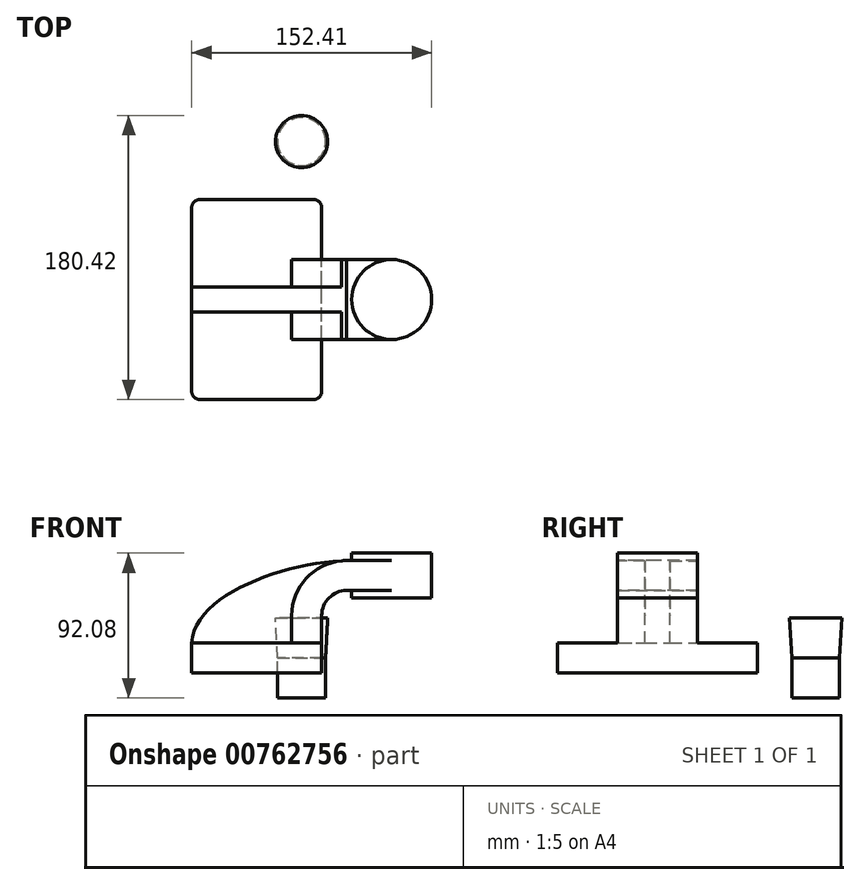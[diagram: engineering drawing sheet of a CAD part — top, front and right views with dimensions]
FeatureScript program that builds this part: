
annotation { "Feature Type Name" : "Feature", "Feature Type Description" : "" }
export const myFeature = defineFeature(function(context is Context, id is Id, definition is map)
    precondition{}
    {
        {
            var Q0;
            Q0=qCreatedBy(makeId("Front.planeOp"),FACE);
            var sketch = newSketch(context, id + "F0", { "sketchPlane" : qUnion([Q0])});
            skLineSegment(sketch, "E0.rect.bottom", {"start": v(-41.28, 9.52) * mm, "end": v(41.28, 9.52) * mm});
            skLineSegment(sketch, "E0.rect.top", {"start": v(-41.28, -9.52) * mm, "end": v(41.28, -9.52) * mm});
            skLineSegment(sketch, "E0.rect.left", {"start": v(-41.28, 9.52) * mm, "end": v(-41.28, -9.52) * mm});
            skLineSegment(sketch, "E0.rect.right", {"start": v(41.28, 9.52) * mm, "end": v(41.28, -9.52) * mm});
            skPoint(sketch, "E0.rect.middle", {"position": v(0, 0) * mm});
            skLineSegment(sketch, "E1", {"start": v(41.28, 9.52) * mm, "end": v(41.28, 27) * mm});
            skArc(sketch, "E2", {"start": v(41.28, 27) * mm, "mid": v(45.92, 38.23) * mm, "end": v(57.15, 42.88) * mm});
            skLineSegment(sketch, "E3", {"start": v(57.15, 42.88) * mm, "end": v(85.72, 42.88) * mm});
            skLineSegment(sketch, "E4.rect.bottom", {"start": v(60.32, 38.1) * mm, "end": v(111.12, 38.1) * mm});
            skLineSegment(sketch, "E4.rect.top", {"start": v(60.32, 66.68) * mm, "end": v(111.12, 66.68) * mm});
            skLineSegment(sketch, "E4.rect.left", {"start": v(60.32, 38.1) * mm, "end": v(60.32, 66.68) * mm});
            skLineSegment(sketch, "E4.rect.right", {"start": v(111.13, 38.1) * mm, "end": v(111.12, 66.68) * mm});
            skPoint(sketch, "E4.rect.middle", {"position": v(85.72, 52.39) * mm});
            skLineSegment(sketch, "E5.0", {"start": v(57.15, 61.93) * mm, "end": v(85.72, 61.93) * mm});
            skArc(sketch, "E5.1", {"start": v(22.23, 27) * mm, "mid": v(32.45, 51.7) * mm, "end": v(57.15, 61.93) * mm});
            skLineSegment(sketch, "E5.2", {"start": v(22.23, 9.52) * mm, "end": v(22.23, 27) * mm});
            skLineSegment(sketch, "E6", {"start": v(85.72, 38.1) * mm, "end": v(85.72, 66.68) * mm});
            skFitSpline(sketch, "E7", {"points": [v(-41.28, 9.53) * mm, v(57.15, 61.93) * mm], "startDerivative": vector(5.2, 92.34) * mm, "endDerivative": vector(120.92, 4.22) * mm});
            skSolve(sketch);
        }
        {
            var Q0;
            Q0=makeQuery(id+"F0.imprint","IMPRINT",FACE,{"disambiguationData":[TD([[makeQuery(id+"F0.imprint","IMPRINT",EDGE,{"derivedFrom":sQuery(id+"F0.wireOp",EDGE,"E0.rect.top")}),1.0]])]});
            extrude(context, id + "F1", {"entities" : qUnion([Q0]), "endBound" : BoundingType.SYMMETRIC, "depth" : 127 * mm});
        }
        {
            var Q0;
            {var subQ9=sQuery(id+"F0.wireOp",EDGE,"E1");Q0=makeQuery(id+"F0.imprint","IMPRINT",FACE,{"disambiguationData":[TD([[makeQuery(id+"F0.imprint","IMPRINT",EDGE,{"derivedFrom":subQ9}),1.0]])]});}
            var Q1;
            {var subQ0=sQuery(id+"F0.wireOp",EDGE,"E6");var subQ1=sQuery(id+"F0.wireOp",EDGE,"E3");var subQ2=makeQuery(id+"F0.imprint","INTERSECT",VERTEX,{"derivedFrom":[subQ1,subQ0]});Q1=makeQuery(id+"F0.imprint","IMPRINT",FACE,{"disambiguationData":[TD([[makeQuery(id+"F0.imprint","IMPRINT",EDGE,{"disambiguationData":[TD([[subQ2,1.0]])],"derivedFrom":subQ1}),1.0]])]});}
            extrude(context, id + "F2", {"entities" : qUnion([Q0, Q1]), "operationType" : NewBodyOperationType.ADD, "endBound" : BoundingType.SYMMETRIC, "depth" : 50.8 * mm});
        }
        {
            var Q0;
            {var subQ3=sQuery(id+"F0.wireOp",EDGE,"E5.2");Q0=makeQuery(id+"F0.imprint","IMPRINT",FACE,{"disambiguationData":[TD([[makeQuery(id+"F0.imprint","IMPRINT",EDGE,{"derivedFrom":subQ3}),1.0]])]});}
            extrude(context, id + "F3", {"entities" : qUnion([Q0]), "operationType" : NewBodyOperationType.ADD, "endBound" : BoundingType.SYMMETRIC, "depth" : 15.88 * mm});
        }
        {
            var Q0;
            {var subQ5=sQuery(id+"F0.wireOp",EDGE,"E4.rect.right");Q0=makeQuery(id+"F0.imprint","IMPRINT",FACE,{"disambiguationData":[TD([[makeQuery(id+"F0.imprint","IMPRINT",EDGE,{"derivedFrom":subQ5}),1.0]])]});}
            var Q1;
            Q1=sQuery(id+"F0.wireOp",EDGE,"E6");
            revolve(context, id + "F4", {"operationType" : NewBodyOperationType.ADD, "entities" : qUnion([Q0]), "axis" : qUnion([Q1]), "revolveType" : RevolveType.FULL});
        }
        {
            var Q0;
            Q0=makeQuery(id+"F1.opExtrude","CAP_EDGE",EDGE,{"disambiguationData":[OSD([sQuery(id+"F0.wireOp",EDGE,"E0.rect.right")])],"isStart":false});
            var Q1;
            Q1=makeQuery(id+"F1.opExtrude","CAP_EDGE",EDGE,{"disambiguationData":[OSD([sQuery(id+"F0.wireOp",EDGE,"E0.rect.left")])],"isStart":false});
            var Q2;
            Q2=makeQuery(id+"F1.opExtrude","CAP_EDGE",EDGE,{"disambiguationData":[OSD([sQuery(id+"F0.wireOp",EDGE,"E0.rect.right")])],"isStart":true});
            var Q3;
            Q3=makeQuery(id+"F1.opExtrude","CAP_EDGE",EDGE,{"disambiguationData":[OSD([sQuery(id+"F0.wireOp",EDGE,"E0.rect.left")])],"isStart":true});
            fillet(context, id + "F5", {"entities" : qUnion([Q0, Q1, Q2, Q3]), "radius" : 5.08 * mm, "tangentPropagation" : true, "allowEdgeOverflow" : false});
        }
        {
            var Q0;
            Q0=qCreatedBy(makeId("Top.planeOp"),FACE);
            var sketch = newSketch(context, id + "F6", { "sketchPlane" : qUnion([Q0])});
            skCircle(sketch, "E8", {"center": v(28.52, 100.38) * mm, "radius": 15.21 * mm});
            skSolve(sketch);
        }
        {
            var Q0;
            Q0 = qSketchRegion(id + "F6", true);
            extrude(context, id + "F7", {"entities" : qUnion([Q0]), "oppositeDirection" : true, "depth" : 25.4 * mm, "offsetDistance" : 25.4 * mm, "hasSecondDirection" : true, "secondDirectionOppositeDirection" : false, "secondDirectionDepth" : 25.4 * mm, "hasSecondDirectionDraft" : true, "secondDirectionDraftAngle" : 3 * degree});
        }
    });
